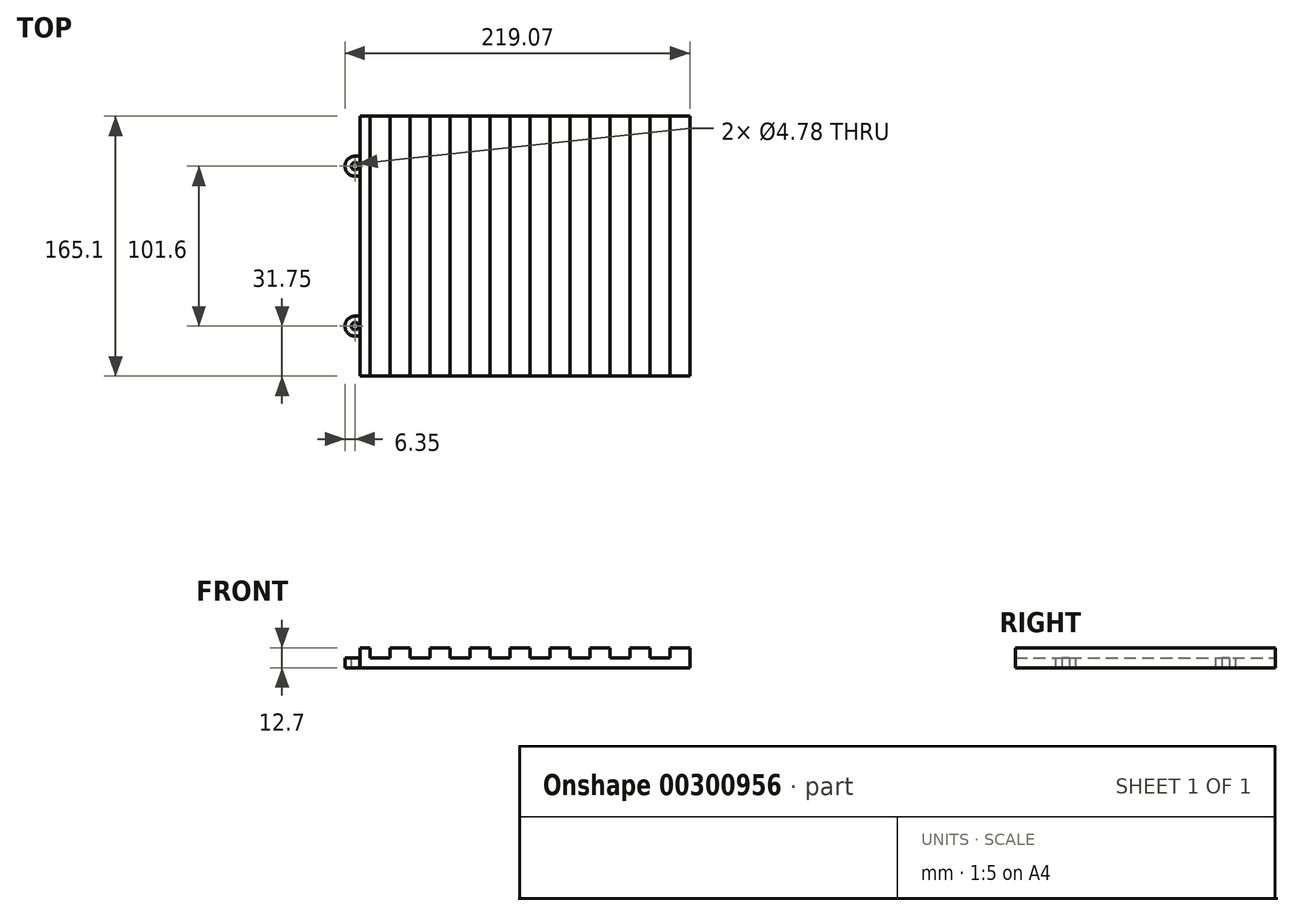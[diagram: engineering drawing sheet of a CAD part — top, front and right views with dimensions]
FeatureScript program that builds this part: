
annotation { "Feature Type Name" : "Feature", "Feature Type Description" : "" }
export const myFeature = defineFeature(function(context is Context, id is Id, definition is map)
    precondition{}
    {
        {
            var Q0;
            Q0=qCreatedBy(makeId("Front.planeOp"),FACE);
            var sketch = newSketch(context, id + "F0", { "sketchPlane" : qUnion([Q0])});
            skLineSegment(sketch, "E0.bottom", {"start": v(-104.78, 0) * mm, "end": v(104.78, 0) * mm});
            skLineSegment(sketch, "E0.top", {"start": v(-104.78, 12.7) * mm, "end": v(-98.43, 12.7) * mm});
            skLineSegment(sketch, "E0.left", {"start": v(-104.78, 0) * mm, "end": v(-104.78, 12.7) * mm});
            skLineSegment(sketch, "E0.right", {"start": v(104.78, 0) * mm, "end": v(104.78, 12.7) * mm});
            skLineSegment(sketch, "E1", {"start": v(-98.43, 12.7) * mm, "end": v(-98.43, 6.35) * mm});
            skLineSegment(sketch, "E2", {"start": v(-98.43, 6.35) * mm, "end": v(-85.73, 6.35) * mm});
            skLineSegment(sketch, "E3", {"start": v(-85.73, 6.35) * mm, "end": v(-85.73, 12.7) * mm});
            skLineSegment(sketch, "E4.trimOffspring", {"start": v(-85.73, 12.7) * mm, "end": v(-73.03, 12.7) * mm});
            skLineSegment(sketch, "E5.1.0.0", {"start": v(-73.03, 12.7) * mm, "end": v(-73.03, 6.35) * mm});
            skLineSegment(sketch, "E5.1.0.1", {"start": v(-73.03, 6.35) * mm, "end": v(-60.33, 6.35) * mm});
            skLineSegment(sketch, "E5.1.0.2", {"start": v(-60.33, 6.35) * mm, "end": v(-60.33, 12.7) * mm});
            skLineSegment(sketch, "E5.2.0.0", {"start": v(-47.63, 12.7) * mm, "end": v(-47.63, 6.35) * mm});
            skLineSegment(sketch, "E5.2.0.1", {"start": v(-47.63, 6.35) * mm, "end": v(-34.93, 6.35) * mm});
            skLineSegment(sketch, "E5.2.0.2", {"start": v(-34.93, 6.35) * mm, "end": v(-34.93, 12.7) * mm});
            skLineSegment(sketch, "E5.3.0.0", {"start": v(-22.23, 12.7) * mm, "end": v(-22.23, 6.35) * mm});
            skLineSegment(sketch, "E5.3.0.1", {"start": v(-22.23, 6.35) * mm, "end": v(-9.53, 6.35) * mm});
            skLineSegment(sketch, "E5.3.0.2", {"start": v(-9.53, 6.35) * mm, "end": v(-9.53, 12.7) * mm});
            skLineSegment(sketch, "E5.4.0.0", {"start": v(3.17, 12.7) * mm, "end": v(3.17, 6.35) * mm});
            skLineSegment(sketch, "E5.4.0.1", {"start": v(3.17, 6.35) * mm, "end": v(15.87, 6.35) * mm});
            skLineSegment(sketch, "E5.4.0.2", {"start": v(15.87, 6.35) * mm, "end": v(15.87, 12.7) * mm});
            skLineSegment(sketch, "E5.5.0.0", {"start": v(28.57, 12.7) * mm, "end": v(28.57, 6.35) * mm});
            skLineSegment(sketch, "E5.5.0.1", {"start": v(28.57, 6.35) * mm, "end": v(41.27, 6.35) * mm});
            skLineSegment(sketch, "E5.5.0.2", {"start": v(41.27, 6.35) * mm, "end": v(41.27, 12.7) * mm});
            skLineSegment(sketch, "E5.6.0.0", {"start": v(53.97, 12.7) * mm, "end": v(53.97, 6.35) * mm});
            skLineSegment(sketch, "E5.6.0.1", {"start": v(53.97, 6.35) * mm, "end": v(66.67, 6.35) * mm});
            skLineSegment(sketch, "E5.6.0.2", {"start": v(66.67, 6.35) * mm, "end": v(66.67, 12.7) * mm});
            skLineSegment(sketch, "E5.direction1", {"start": v(-98.43, 6.35) * mm, "end": v(-73.03, 6.35) * mm, "construction": true});
            skLineSegment(sketch, "E6.trimOffspring", {"start": v(-60.33, 12.7) * mm, "end": v(-47.63, 12.7) * mm});
            skLineSegment(sketch, "E7.trimOffspring", {"start": v(-34.93, 12.7) * mm, "end": v(-22.23, 12.7) * mm});
            skLineSegment(sketch, "E8.trimOffspring", {"start": v(-9.53, 12.7) * mm, "end": v(3.17, 12.7) * mm});
            skLineSegment(sketch, "E9.trimOffspring", {"start": v(15.87, 12.7) * mm, "end": v(28.57, 12.7) * mm});
            skLineSegment(sketch, "E10.trimOffspring", {"start": v(41.27, 12.7) * mm, "end": v(53.97, 12.7) * mm});
            skLineSegment(sketch, "E11.trimOffspring", {"start": v(66.67, 12.7) * mm, "end": v(79.37, 12.7) * mm});
            skLineSegment(sketch, "E12.trimOffspring", {"start": v(92.07, 12.7) * mm, "end": v(104.78, 12.7) * mm});
            skLineSegment(sketch, "E13.0.7.0", {"start": v(79.37, 12.7) * mm, "end": v(79.37, 6.35) * mm});
            skLineSegment(sketch, "E13.3.7.0", {"start": v(79.37, 6.35) * mm, "end": v(92.07, 6.35) * mm});
            skLineSegment(sketch, "E13.6.7.0", {"start": v(92.07, 6.35) * mm, "end": v(92.07, 12.7) * mm});
            skSolve(sketch);
        }
        {
            var Q0;
            Q0=qSketchRegion(id+"F0",true);
            extrude(context, id + "F1", {"entities" : qUnion([Q0]), "depth" : 165.1 * mm});
        }
        {
            var Q0;
            Q0=makeQuery(id+"F1.opExtrude","SWEPT_FACE",FACE,{"disambiguationData":[OSD([sQuery(id+"F0.wireOp",EDGE,"E0.bottom")])]});
            var sketch = newSketch(context, id + "F2", { "sketchPlane" : qUnion([Q0])});
            skLineSegment(sketch, "E14", {"start": v(-104.78, 82.55) * mm, "end": v(104.78, 82.55) * mm, "construction": true});
            skLineSegment(sketch, "E15", {"start": v(0, 165.1) * mm, "end": v(0, 0) * mm, "construction": true});
            skCircle(sketch, "E16.MirrorC", {"center": v(-107.95, 31.75) * mm, "radius": 2.39 * mm});
            skLineSegment(sketch, "E17.MirrorCS", {"start": v(-104.78, 25.4) * mm, "end": v(-107.95, 25.4) * mm});
            skLineSegment(sketch, "E18.MirrorCS", {"start": v(-104.78, 38.1) * mm, "end": v(-107.95, 38.1) * mm});
            skLineSegment(sketch, "E19.MirrorCS", {"start": v(-104.78, 25.4) * mm, "end": v(-104.78, 38.1) * mm});
            skArc(sketch, "E20.MirrorCS", {"start": v(-107.95, 38.1) * mm, "mid": v(-114.3, 31.75) * mm, "end": v(-107.95, 25.4) * mm});
            skArc(sketch, "E21.MirrorCS", {"start": v(-107.95, 127) * mm, "mid": v(-114.3, 133.35) * mm, "end": v(-107.95, 139.7) * mm});
            skCircle(sketch, "E22.MirrorC", {"center": v(-107.95, 133.35) * mm, "radius": 2.39 * mm});
            skLineSegment(sketch, "E23.MirrorCS", {"start": v(-104.78, 127) * mm, "end": v(-107.95, 127) * mm});
            skLineSegment(sketch, "E24.MirrorCS", {"start": v(-104.78, 139.7) * mm, "end": v(-107.95, 139.7) * mm});
            skLineSegment(sketch, "E25.MirrorCS", {"start": v(-104.78, 139.7) * mm, "end": v(-104.78, 127) * mm});
            skSolve(sketch);
        }
        {
            var Q0;
            Q0=qSketchRegion(id+"F2",true);
            extrude(context, id + "F3", {"entities" : qUnion([Q0]), "operationType" : NewBodyOperationType.ADD, "oppositeDirection" : true, "depth" : 6.35 * mm});
        }
    });
